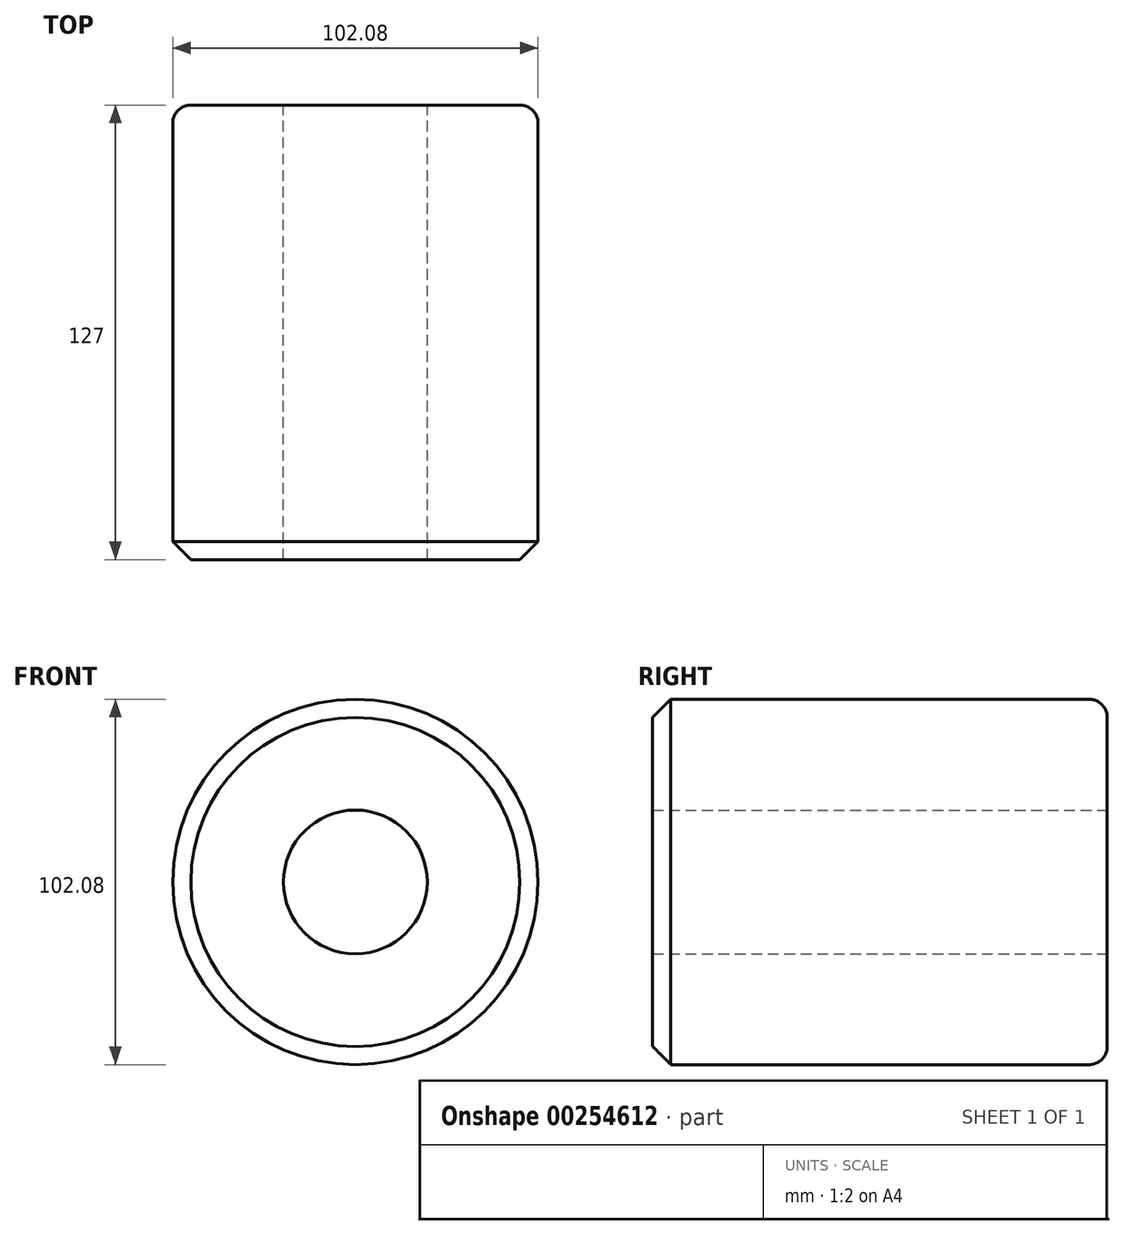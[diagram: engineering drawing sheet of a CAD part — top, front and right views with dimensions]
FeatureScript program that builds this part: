
annotation { "Feature Type Name" : "Feature", "Feature Type Description" : "" }
export const myFeature = defineFeature(function(context is Context, id is Id, definition is map)
    precondition{}
    {
        {
            var Q0;
            Q0=qCreatedBy(makeId("Front.planeOp"),FACE);
            var sketch = newSketch(context, id + "F0", { "sketchPlane" : qUnion([Q0])});
            skCircle(sketch, "E0", {"center": v(0, 0) * mm, "radius": 51.04 * mm});
            skSolve(sketch);
        }
        {
            var Q0;
            Q0 = qSketchRegion(id + "F0", true);
            extrude(context, id + "F1", {"entities" : qUnion([Q0]), "endBound" : BoundingType.SYMMETRIC, "depth" : 127 * mm});
        }
        {
            var Q0;
            Q0=makeQuery(id+"F1.opExtrude","CAP_EDGE",EDGE,{"disambiguationData":[OSD([sQuery(id+"F0.wireOp",EDGE,"E0")])],"isStart":false});
            chamfer(context, id + "F2", {"entities" : qUnion([Q0]), "width" : 5.08 * mm, "tangentPropagation" : true});
        }
        {
            var Q0;
            Q0=makeQuery(id+"F1.opExtrude","CAP_EDGE",EDGE,{"disambiguationData":[OSD([sQuery(id+"F0.wireOp",EDGE,"E0")])],"isStart":true});
            var Q1;
            Q1=makeQuery(id+"F1.opExtrude","CAP_FACE",FACE,{"disambiguationData":[OSD([sQuery(id+"F0.wireOp",EDGE,"E0")])],"isStart":true});
            fillet(context, id + "F3", {"entities" : qUnion([Q0, Q1]), "radius" : 5.08 * mm, "tangentPropagation" : true, "allowEdgeOverflow" : false});
        }
        {
            var Q0;
            Q0=makeQuery(id+"F1.opExtrude","CAP_FACE",FACE,{"disambiguationData":[OSD([sQuery(id+"F0.wireOp",EDGE,"E0")])],"isStart":true});
            var sketch = newSketch(context, id + "F4", { "sketchPlane" : qUnion([Q0])});
            skCircle(sketch, "E1", {"center": v(0, 0) * mm, "radius": 20.08 * mm});
            skSolve(sketch);
        }
        {
            var Q0;
            Q0=makeQuery(id+"F4.imprint","IMPRINT",FACE,{"disambiguationData":[TD([[makeQuery(id+"F4.imprint","IMPRINT",EDGE,{"derivedFrom":sQuery(id+"F4.wireOp",EDGE,"E1")}),1.0]])]});
            extrude(context, id + "F5", {"entities" : qUnion([Q0]), "operationType" : NewBodyOperationType.REMOVE, "endBound" : BoundingType.THROUGH_ALL, "oppositeDirection" : true, "depth" : 25.4 * mm});
        }
    });
